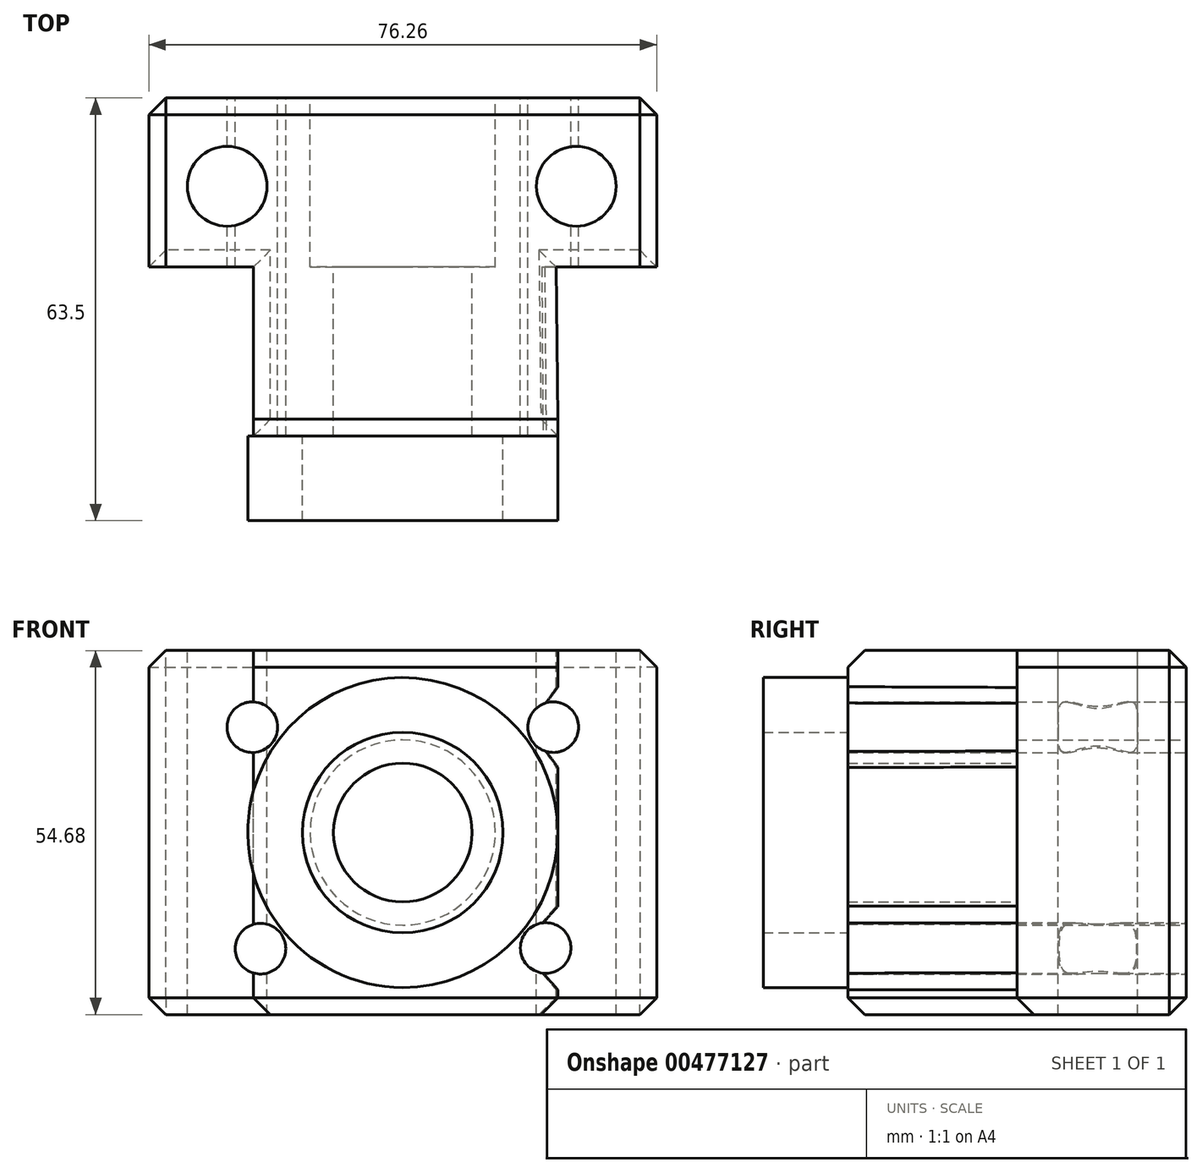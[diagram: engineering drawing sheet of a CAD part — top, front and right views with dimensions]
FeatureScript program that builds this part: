
annotation { "Feature Type Name" : "Feature", "Feature Type Description" : "" }
export const myFeature = defineFeature(function(context is Context, id is Id, definition is map)
    precondition{}
    {
        {
            var Q0;
            Q0=qCreatedBy(makeId("Front.planeOp"),FACE);
            var sketch = newSketch(context, id + "F0", { "sketchPlane" : qUnion([Q0])});
            skLineSegment(sketch, "E0.bottom", {"start": v(38.13, 27.34) * mm, "end": v(-38.13, 27.34) * mm});
            skLineSegment(sketch, "E0.top", {"start": v(38.13, -27.34) * mm, "end": v(-38.13, -27.34) * mm});
            skLineSegment(sketch, "E0.left", {"start": v(38.13, 27.34) * mm, "end": v(38.13, -27.34) * mm});
            skLineSegment(sketch, "E0.right", {"start": v(-38.13, 27.34) * mm, "end": v(-38.13, -27.34) * mm});
            skPoint(sketch, "E0.middle", {"position": v(0, 0) * mm});
            skCircle(sketch, "E1", {"center": v(-22.6, 15.83) * mm, "radius": 3.8 * mm});
            skCircle(sketch, "E2", {"center": v(22.6, 15.83) * mm, "radius": 3.8 * mm});
            skCircle(sketch, "E3", {"center": v(-21.37, -17.44) * mm, "radius": 3.8 * mm});
            skCircle(sketch, "E4", {"center": v(21.46, -17.34) * mm, "radius": 3.8 * mm});
            skSolve(sketch);
        }
        {
            var Q0;
            Q0 = qSketchRegion(id + "F0", true);
            extrude(context, id + "F1", {"entities" : qUnion([Q0]), "depth" : 50.8 * mm});
        }
        {
            var Q0;
            Q0 = qSketchRegion(id + "F0", true);
            extrude(context, id + "F2", {"entities" : qUnion([Q0]), "operationType" : NewBodyOperationType.REMOVE, "oppositeDirection" : true, "depth" : 50.8 * mm});
        }
        {
            var Q0;
            Q0=makeQuery(id+"F1.opExtrude","CAP_FACE",FACE,{"disambiguationData":[OSD([sQuery(id+"F0.wireOp",EDGE,"E0.bottom"),sQuery(id+"F0.wireOp",EDGE,"E0.top"),sQuery(id+"F0.wireOp",EDGE,"E0.left"),sQuery(id+"F0.wireOp",EDGE,"E0.right"),sQuery(id+"F0.wireOp",EDGE,"E1"),sQuery(id+"F0.wireOp",EDGE,"E2"),sQuery(id+"F0.wireOp",EDGE,"E3"),sQuery(id+"F0.wireOp",EDGE,"E4")])],"isStart":false});
            var sketch = newSketch(context, id + "F3", { "sketchPlane" : qUnion([Q0])});
            skCircle(sketch, "E5", {"center": v(0, 0) * mm, "radius": 23.28 * mm});
            skCircle(sketch, "E6", {"center": v(0, 0) * mm, "radius": 9.61 * mm});
            skCircle(sketch, "E7", {"center": v(0, 0) * mm, "radius": 15.05 * mm});
            skCircle(sketch, "E8", {"center": v(0, 0) * mm, "radius": 9.62 * mm});
            skSolve(sketch);
        }
        {
            var Q0;
            Q0 = qSketchRegion(id + "F3", true);
            var Q1;
            Q1=makeQuery(id+"F3.imprint","IMPRINT",FACE,{"disambiguationData":[TD([[makeQuery(id+"F3.imprint","IMPRINT",EDGE,{"derivedFrom":sQuery(id+"F3.wireOp",EDGE,"E6")}),1.0]])]});
            extrude(context, id + "F4", {"entities" : qUnion([Q0, Q1]), "operationType" : NewBodyOperationType.ADD, "depth" : 12.7 * mm});
        }
        {
            var Q0;
            Q0=makeQuery(id+"F1.opExtrude","SWEPT_FACE",FACE,{"disambiguationData":[OSD([sQuery(id+"F0.wireOp",EDGE,"E0.bottom")])]});
            var sketch = newSketch(context, id + "F5", { "sketchPlane" : qUnion([Q0])});
            skCircle(sketch, "E9", {"center": v(-26.37, -13.26) * mm, "radius": 5.99 * mm});
            skCircle(sketch, "E10", {"center": v(26.06, -13.26) * mm, "radius": 5.99 * mm});
            skLineSegment(sketch, "E11", {"start": v(-38.13, -25.4) * mm, "end": v(-22.4, -25.4) * mm});
            skLineSegment(sketch, "E12", {"start": v(-22.4, -25.4) * mm, "end": v(-22.4, -50.8) * mm});
            skLineSegment(sketch, "E13", {"start": v(23.32, -50.8) * mm, "end": v(38.13, -50.8) * mm});
            skLineSegment(sketch, "E14", {"start": v(38.13, -50.8) * mm, "end": v(38.13, -25.4) * mm});
            skLineSegment(sketch, "E15", {"start": v(38.13, -25.4) * mm, "end": v(23.01, -25.4) * mm});
            skLineSegment(sketch, "E16", {"start": v(23.01, -25.4) * mm, "end": v(23.32, -50.8) * mm});
            skSolve(sketch);
        }
        {
            var Q0;
            Q0 = qSketchRegion(id + "F5", true);
            var Q1;
            {var subQ0=sQuery(id+"F5.wireOp",EDGE,"E11");Q1=makeQuery(id+"F5.imprint","IMPRINT",FACE,{"disambiguationData":[TD([[makeQuery(id+"F5.imprint","IMPRINT",EDGE,{"derivedFrom":subQ0}),-1.0]])]});}
            extrude(context, id + "F6", {"entities" : qUnion([Q0, Q1]), "operationType" : NewBodyOperationType.REMOVE, "oppositeDirection" : true, "depth" : 63.5 * mm});
        }
        {
            var Q0;
            Q0=makeQuery(id+"F1.opExtrude","CAP_FACE",FACE,{"disambiguationData":[OSD([sQuery(id+"F0.wireOp",EDGE,"E0.bottom"),sQuery(id+"F0.wireOp",EDGE,"E0.top"),sQuery(id+"F0.wireOp",EDGE,"E0.left"),sQuery(id+"F0.wireOp",EDGE,"E0.right"),sQuery(id+"F0.wireOp",EDGE,"E1"),sQuery(id+"F0.wireOp",EDGE,"E2"),sQuery(id+"F0.wireOp",EDGE,"E3"),sQuery(id+"F0.wireOp",EDGE,"E4")])],"isStart":true});
            var sketch = newSketch(context, id + "F7", { "sketchPlane" : qUnion([Q0])});
            skCircle(sketch, "E17", {"center": v(0, 0) * mm, "radius": 10.41 * mm});
            skSolve(sketch);
        }
        {
            var Q0;
            Q0 = qSketchRegion(id + "F7", true);
            extrude(context, id + "F8", {"entities" : qUnion([Q0]), "operationType" : NewBodyOperationType.REMOVE, "oppositeDirection" : true, "depth" : 76.2 * mm});
        }
        {
            var Q0;
            Q0=makeQuery(id+"F1.opExtrude","CAP_FACE",FACE,{"disambiguationData":[OSD([sQuery(id+"F0.wireOp",EDGE,"E0.bottom"),sQuery(id+"F0.wireOp",EDGE,"E0.top"),sQuery(id+"F0.wireOp",EDGE,"E0.left"),sQuery(id+"F0.wireOp",EDGE,"E0.right"),sQuery(id+"F0.wireOp",EDGE,"E1"),sQuery(id+"F0.wireOp",EDGE,"E2"),sQuery(id+"F0.wireOp",EDGE,"E3"),sQuery(id+"F0.wireOp",EDGE,"E4")])],"isStart":true});
            var sketch = newSketch(context, id + "F9", { "sketchPlane" : qUnion([Q0])});
            skCircle(sketch, "E18", {"center": v(0, 0) * mm, "radius": 13.9 * mm});
            skSolve(sketch);
        }
        {
            var Q0;
            Q0 = qSketchRegion(id + "F9", true);
            extrude(context, id + "F10", {"entities" : qUnion([Q0]), "operationType" : NewBodyOperationType.REMOVE, "oppositeDirection" : true, "depth" : 25.4 * mm});
        }
        {
            var Q0;
            Q0=makeQuery(id+"F1.opExtrude","CAP_EDGE",EDGE,{"disambiguationData":[OSD([sQuery(id+"F0.wireOp",EDGE,"E0.right")])],"isStart":true});
            var Q1;
            Q1=makeQuery(id+"F1.opExtrude","CAP_EDGE",EDGE,{"disambiguationData":[OSD([sQuery(id+"F0.wireOp",EDGE,"E0.top")])],"isStart":true});
            var Q2;
            Q2=makeQuery(id+"F1.opExtrude","CAP_EDGE",EDGE,{"disambiguationData":[OSD([sQuery(id+"F0.wireOp",EDGE,"E0.left")])],"isStart":true});
            var Q3;
            Q3=makeQuery(id+"F1.opExtrude","CAP_EDGE",EDGE,{"disambiguationData":[OSD([sQuery(id+"F0.wireOp",EDGE,"E0.bottom")])],"isStart":true});
            var Q4;
            Q4=makeQuery(id+"F1.opExtrude","SWEPT_EDGE",EDGE,{"disambiguationData":[OSD([sQuery(id+"F0.wireOp",EDGE,"E0.bottom"),sQuery(id+"F0.wireOp",EDGE,"E0.right")])]});
            var Q5;
            Q5=makeQuery(id+"F1.opExtrude","SWEPT_EDGE",EDGE,{"disambiguationData":[OSD([sQuery(id+"F0.wireOp",EDGE,"E0.top"),sQuery(id+"F0.wireOp",EDGE,"E0.right")])]});
            var Q6;
            Q6=makeQuery(id+"F1.opExtrude","SWEPT_EDGE",EDGE,{"disambiguationData":[OSD([sQuery(id+"F0.wireOp",EDGE,"E0.bottom"),sQuery(id+"F0.wireOp",EDGE,"E0.left")])]});
            var Q7;
            Q7=makeQuery(id+"F6.boolean.opBoolean","COPY",EDGE,{"derivedFrom":makeQuery(id+"F6.opExtrude","CAP_EDGE",EDGE,{"disambiguationData":[OSD([sQuery(id+"F5.wireOp",EDGE,"E15")])],"isStart":true})});
            var Q8;
            Q8=makeQuery(id+"F6.boolean.opBoolean","INTERSECT",EDGE,{"disambiguationData":[OD(0.0)],"derivedFrom":[makeQuery(id+"F1.opExtrude","SWEPT_FACE",FACE,{"disambiguationData":[OSD([sQuery(id+"F0.wireOp",EDGE,"E2")])]}),makeQuery(id+"F6.opExtrude","SWEPT_FACE",FACE,{"disambiguationData":[OSD([sQuery(id+"F5.wireOp",EDGE,"E16")])]})]});
            var Q9;
            Q9=makeQuery(id+"F6.boolean.opBoolean","INTERSECT",EDGE,{"disambiguationData":[OD(1.0)],"derivedFrom":[makeQuery(id+"F1.opExtrude","SWEPT_FACE",FACE,{"disambiguationData":[OSD([sQuery(id+"F0.wireOp",EDGE,"E2")])]}),makeQuery(id+"F6.opExtrude","SWEPT_FACE",FACE,{"disambiguationData":[OSD([sQuery(id+"F5.wireOp",EDGE,"E16")])]})]});
            var Q10;
            Q10=makeQuery(id+"F6.boolean.opBoolean","INTERSECT",EDGE,{"disambiguationData":[OD(1.0)],"derivedFrom":[makeQuery(id+"F1.opExtrude","SWEPT_FACE",FACE,{"disambiguationData":[OSD([sQuery(id+"F0.wireOp",EDGE,"E4")])]}),makeQuery(id+"F6.opExtrude","SWEPT_FACE",FACE,{"disambiguationData":[OSD([sQuery(id+"F5.wireOp",EDGE,"E16")])]})]});
            var Q11;
            Q11=makeQuery(id+"F6.boolean.opBoolean","INTERSECT",EDGE,{"disambiguationData":[OD(0.0)],"derivedFrom":[makeQuery(id+"F1.opExtrude","SWEPT_FACE",FACE,{"disambiguationData":[OSD([sQuery(id+"F0.wireOp",EDGE,"E4")])]}),makeQuery(id+"F6.opExtrude","SWEPT_FACE",FACE,{"disambiguationData":[OSD([sQuery(id+"F5.wireOp",EDGE,"E16")])]})]});
            var Q12;
            Q12=makeQuery(id+"F6.boolean.opBoolean","INTERSECT",EDGE,{"derivedFrom":[makeQuery(id+"F1.opExtrude","SWEPT_FACE",FACE,{"disambiguationData":[OSD([sQuery(id+"F0.wireOp",EDGE,"E0.top")])]}),makeQuery(id+"F6.opExtrude","SWEPT_FACE",FACE,{"disambiguationData":[OSD([sQuery(id+"F5.wireOp",EDGE,"E16")])]})]});
            var Q13;
            Q13=makeQuery(id+"F1.opExtrude","CAP_EDGE",EDGE,{"disambiguationData":[OSD([sQuery(id+"F0.wireOp",EDGE,"E0.bottom")])],"isStart":false});
            var Q14;
            Q14=makeQuery(id+"F6.boolean.opBoolean","COPY",EDGE,{"derivedFrom":makeQuery(id+"F6.opExtrude","CAP_EDGE",EDGE,{"disambiguationData":[OSD([sQuery(id+"F5.wireOp",EDGE,"E12")])],"isStart":true})});
            var Q15;
            Q15=makeQuery(id+"F6.boolean.opBoolean","COPY",EDGE,{"derivedFrom":makeQuery(id+"F6.opExtrude","CAP_EDGE",EDGE,{"disambiguationData":[OSD([sQuery(id+"F5.wireOp",EDGE,"E11")])],"isStart":true})});
            var Q16;
            Q16=makeQuery(id+"F6.boolean.opBoolean","COPY",EDGE,{"derivedFrom":makeQuery(id+"F6.opExtrude","CAP_EDGE",EDGE,{"disambiguationData":[OSD([sQuery(id+"F5.wireOp",EDGE,"E16")])],"isStart":true})});
            var Q17;
            Q17=makeQuery(id+"F6.boolean.opBoolean","COPY",EDGE,{"derivedFrom":makeQuery(id+"F6.opExtrude","SWEPT_EDGE",EDGE,{"disambiguationData":[OSD([sQuery(id+"F0.wireOp",EDGE,"E0.bottom"),sQuery(id+"F0.wireOp",EDGE,"E0.right"),sQuery(id+"F5.wireOp",EDGE,"E11")])]})});
            var Q18;
            Q18=makeQuery(id+"F6.boolean.opBoolean","INTERSECT",EDGE,{"derivedFrom":[makeQuery(id+"F1.opExtrude","SWEPT_FACE",FACE,{"disambiguationData":[OSD([sQuery(id+"F0.wireOp",EDGE,"E0.top")])]}),makeQuery(id+"F6.opExtrude","SWEPT_FACE",FACE,{"disambiguationData":[OSD([sQuery(id+"F5.wireOp",EDGE,"E11")])]})]});
            var Q19;
            Q19=makeQuery(id+"F6.boolean.opBoolean","INTERSECT",EDGE,{"derivedFrom":[makeQuery(id+"F1.opExtrude","SWEPT_FACE",FACE,{"disambiguationData":[OSD([sQuery(id+"F0.wireOp",EDGE,"E0.top")])]}),makeQuery(id+"F6.opExtrude","SWEPT_FACE",FACE,{"disambiguationData":[OSD([sQuery(id+"F5.wireOp",EDGE,"E12")])]})]});
            var Q20;
            Q20=makeQuery(id+"F1.opExtrude","CAP_EDGE",EDGE,{"disambiguationData":[OSD([sQuery(id+"F0.wireOp",EDGE,"E0.top")])],"isStart":false});
            var Q21;
            Q21=makeQuery(id+"F6.boolean.opBoolean","INTERSECT",EDGE,{"derivedFrom":[makeQuery(id+"F1.opExtrude","SWEPT_FACE",FACE,{"disambiguationData":[OSD([sQuery(id+"F0.wireOp",EDGE,"E0.top")])]}),makeQuery(id+"F6.opExtrude","SWEPT_FACE",FACE,{"disambiguationData":[OSD([sQuery(id+"F5.wireOp",EDGE,"E15")])]})]});
            var Q22;
            Q22=makeQuery(id+"F1.opExtrude","SWEPT_EDGE",EDGE,{"disambiguationData":[OSD([sQuery(id+"F0.wireOp",EDGE,"E0.top"),sQuery(id+"F0.wireOp",EDGE,"E0.left")])]});
            chamfer(context, id + "F11", {"entities" : qUnion([Q0, Q1, Q2, Q3, Q4, Q5, Q6, Q7, Q8, Q9, Q10, Q11, Q12, Q13, Q14, Q15, Q16, Q17, Q18, Q19, Q20, Q21, Q22]), "width" : 2.54 * mm, "tangentPropagation" : true});
        }
    });
